# Revit family: IS_Tesi_A6559_BIM_ES
name_source: partatom
category: Plumbing Fixtures
revit_build: Autodesk Revit 2017 (Build: 20160225_1515(x64)
units: mm (PartAtom-declared; Revit-internal decimal feet)

## family parameters
Always vertical = No
Cut with Voids When Loaded = No
OmniClass Number = 23.45.55.17
OmniClass Title = Mixing Faucets
Part Type = Normal
Room Calculation Point = No
Round Connector Dimension = Use Diameter
Shared = No
Work Plane-Based = No

## types (1)
- TESI M.LAVABO NORMAL 5L/MIN S/VAL
    Acabado = Cromo
    Accesorios = https://www.idealstandard.es
    AlturaNominal = 72 mm  [stored 0.23622 ft]
    AnchuraNominal = 185 mm  [stored 0.606955 ft]
    Autor = Ideal Standard Iberia
    Ayuda = https://www.idealstandard.es
    Cost = 0 $
    CódigoDeBarras = 4015413338240
    DescripciónUniclass2015 = Washbasin taps
    Description = TESI M.LAVABO NORMAL 5L/MIN S/VAL
    Destacado = TESI M.LAVABO NORMAL 5L/MIN S/VAL
    Dimensiones = 72 x 380 x 185 mm
    DiámetroDeDesagüe = 0
    FechaDeCreación = 01/10/2020
    GarantíaDeLasPiezas = 2
    GarantíaPiezas = 2
    GrosorDelMaterial = 0
    GuíaDeInstallación = https://www.idealstandard.es
    IfcExportaComo = IfcSanitaryTerminalType
    InformaciónDeProducto = https://www.idealstandard.es
    Installation instructions = https://www.idealstandard.es
    LongitudNominal = 380 mm
    Maneta = No
    Manufacturer = https://www.idealstandard.es
    Marca = Ideal Standard Iberia
    Model = A6559AA
    NivelDeDesbordamiento = 0
    Nombre = Washbasintaps_TESI_A6559_IdealStandard
    NombreDeObjetoBim = IS_IdealStandard_Washbasintaps_TESI_A6559
    NúmeroDeModelo = A6559AA
    PesoBruto = 0
    PesoNeto = 1,28
    PlatoDeDucha = No
    Product group = Washbasin manual water supply sets
    ProfundidadNominal = 380 mm
    Referencia = A6559AA
    ReferenciaDeModelo = TESI M.LAVABO NORMAL 5L/MIN S/VAL
    ReferenciaUniclass2015 = Pr_40_20_87_98
    Repuestos = https://www.idealstandard.es
    Revisión = 1
    Teléfono = +34 93 561 80 00
    TestDePresión = 10 bar
    TipoDeConexión = Fontaneria
    TipoDeExportaciónIfc = FAUCET
    TipoDeGarantía = Garantía del fabricante
    URL = https://www.idealstandard.es
    Uniclass 2015 Code = Pr_40_20_87_96
    Uniclass 2015 Name = Washbasin manual water supply sets
    UnidadDeTiempo = Años
    UnidadDeVolúmen = Litros
    UnidadDeÁrea = Milimetros
    UnidadGarantía = Años
    UnidadLineal = Milimetros
    UnidadMonetaria = €
    UrlDelFabricante = https://www.idealstandard.es
    Versión = 1
    VersiónUniclass2015 = v1.1
    ÁreaDeMedición = Interna

note: [stored X ft] marks values corroborated as IEEE doubles in the binary element streams (Revit-internal decimal feet)

## geometry (parser evidence)
native form markers: Sweep x2
no freeform markers — native parametric forms only
